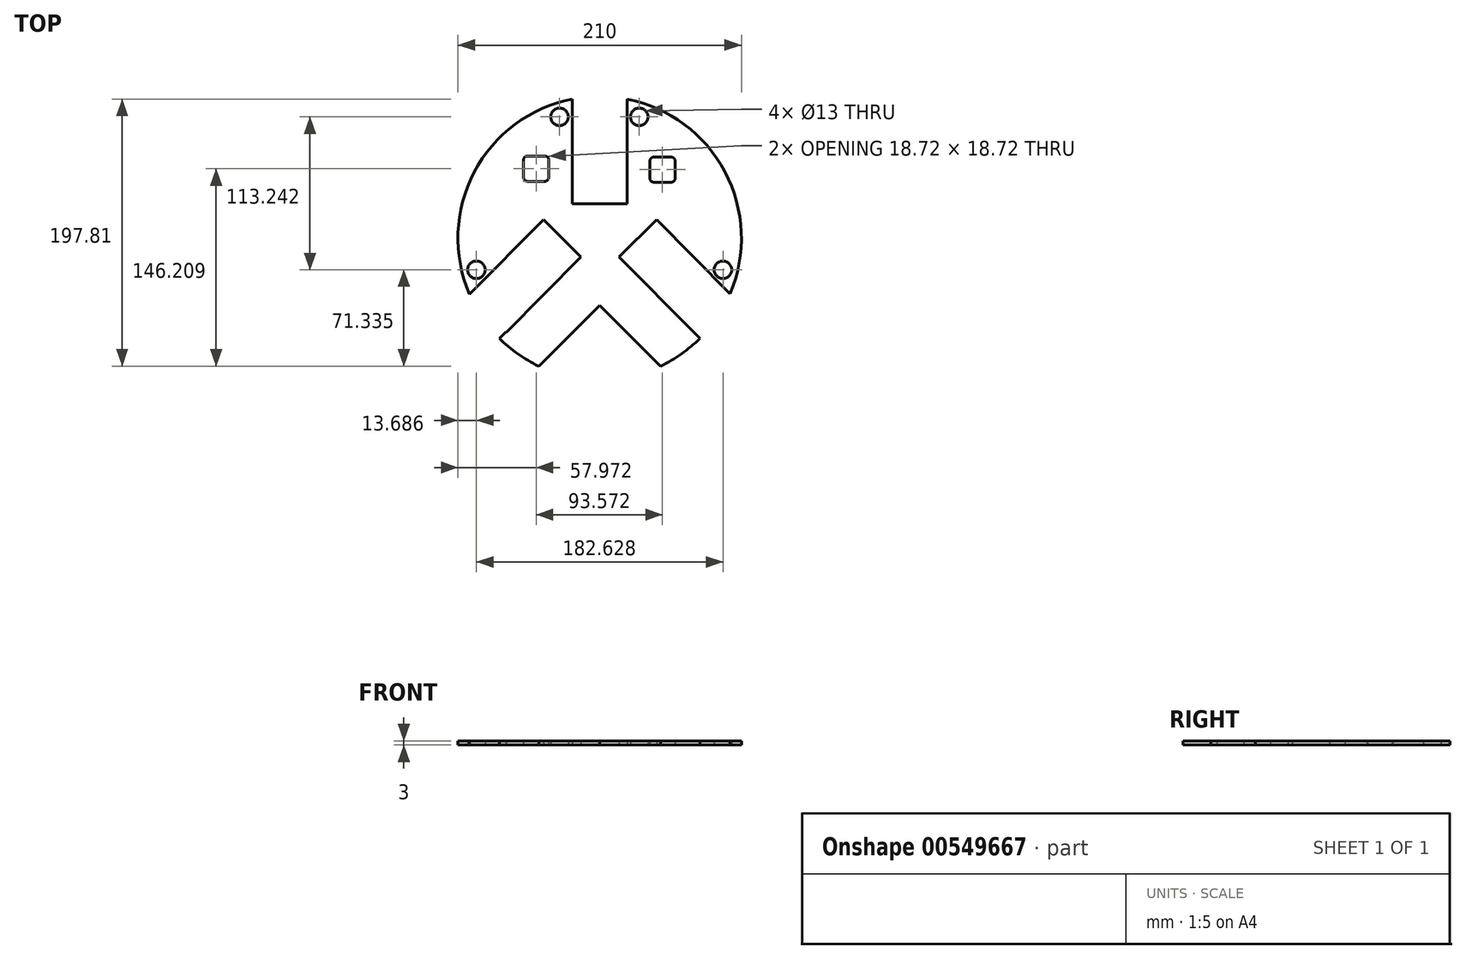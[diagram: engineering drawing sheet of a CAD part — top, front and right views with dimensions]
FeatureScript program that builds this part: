
annotation { "Feature Type Name" : "Feature", "Feature Type Description" : "" }
export const myFeature = defineFeature(function(context is Context, id is Id, definition is map)
    precondition{}
    {
        {
            var Q0;
            Q0=qCreatedBy(makeId("Top.planeOp"),FACE);
            var sketch = newSketch(context, id + "F0", { "sketchPlane" : qUnion([Q0])});
            skCircle(sketch, "E0", {"center": v(0, 0) * mm, "radius": 105 * mm});
            skLineSegment(sketch, "E1", {"start": v(0, 105) * mm, "end": v(0, -105) * mm});
            skLineSegment(sketch, "E2", {"start": v(0, 0) * mm, "end": v(-74.25, -74.25) * mm});
            skLineSegment(sketch, "E3", {"start": v(0, 0) * mm, "end": v(74.25, -74.25) * mm});
            skLineSegment(sketch, "E4", {"start": v(0, 0) * mm, "end": v(0, 105) * mm});
            skLineSegment(sketch, "E5", {"start": v(0, -49.67) * mm, "end": v(-45.13, -94.8) * mm});
            skLineSegment(sketch, "E6", {"start": v(0, -49.67) * mm, "end": v(45.13, -94.8) * mm});
            skLineSegment(sketch, "E7", {"start": v(-20.43, 103.99) * mm, "end": v(-0.4, 103.99) * mm});
            skLineSegment(sketch, "E8.bottom", {"start": v(-20.43, 103.99) * mm, "end": v(20.33, 103.99) * mm});
            skLineSegment(sketch, "E8.top", {"start": v(-20.43, 25.29) * mm, "end": v(20.33, 25.29) * mm});
            skLineSegment(sketch, "E8.left", {"start": v(-20.43, 103.99) * mm, "end": v(-20.43, 25.29) * mm});
            skLineSegment(sketch, "E8.right", {"start": v(20.33, 103.99) * mm, "end": v(20.33, 25.29) * mm});
            skLineSegment(sketch, "E9.bottom", {"start": v(-41.67, 13.74) * mm, "end": v(-13.83, -13.93) * mm});
            skLineSegment(sketch, "E9.top", {"start": v(-97.14, -42.09) * mm, "end": v(-69.3, -69.75) * mm});
            skLineSegment(sketch, "E9.left", {"start": v(-41.67, 13.74) * mm, "end": v(-97.14, -42.09) * mm});
            skLineSegment(sketch, "E9.right", {"start": v(-13.83, -13.93) * mm, "end": v(-69.3, -69.75) * mm});
            skLineSegment(sketch, "E10.bottom", {"start": v(14.3, -13.9) * mm, "end": v(42.15, 13.74) * mm});
            skLineSegment(sketch, "E10.top", {"start": v(69.75, -69.75) * mm, "end": v(97.6, -42.1) * mm});
            skLineSegment(sketch, "E10.left", {"start": v(14.3, -13.9) * mm, "end": v(69.75, -69.75) * mm});
            skLineSegment(sketch, "E10.right", {"start": v(42.15, 13.74) * mm, "end": v(97.6, -42.1) * mm});
            skLineSegment(sketch, "E11.bottom", {"start": v(-53.39, 60.77) * mm, "end": v(-40.67, 60.77) * mm});
            skLineSegment(sketch, "E11.top", {"start": v(-53.39, 42.05) * mm, "end": v(-40.67, 42.05) * mm});
            skLineSegment(sketch, "E11.left", {"start": v(-56.39, 57.77) * mm, "end": v(-56.39, 45.05) * mm});
            skLineSegment(sketch, "E11.right", {"start": v(-37.67, 57.77) * mm, "end": v(-37.67, 45.05) * mm});
            skLineSegment(sketch, "E12.bottom", {"start": v(40.18, 60.07) * mm, "end": v(52.9, 60.07) * mm});
            skLineSegment(sketch, "E12.top", {"start": v(40.18, 41.35) * mm, "end": v(52.9, 41.35) * mm});
            skLineSegment(sketch, "E12.left", {"start": v(37.18, 57.07) * mm, "end": v(37.18, 44.35) * mm});
            skLineSegment(sketch, "E12.right", {"start": v(55.9, 57.07) * mm, "end": v(55.9, 44.35) * mm});
            skCircle(sketch, "E13", {"center": v(-29.72, 89.78) * mm, "radius": 6.5 * mm});
            skCircle(sketch, "E14", {"center": v(29.3, 89.78) * mm, "radius": 6.5 * mm});
            skCircle(sketch, "E15", {"center": v(-91.31, -23.47) * mm, "radius": 6.5 * mm});
            skCircle(sketch, "E16", {"center": v(91.31, -23.47) * mm, "radius": 6.5 * mm});
            skPoint(sketch, "E17.visualSharp", {"position": v(-56.39, 60.77) * mm});
            skArc(sketch, "E17.filletArc", {"start": v(-53.39, 60.77) * mm, "mid": v(-55.5, 59.89) * mm, "end": v(-56.39, 57.77) * mm});
            skPoint(sketch, "E18.visualSharp", {"position": v(-37.67, 60.77) * mm});
            skArc(sketch, "E18.filletArc", {"start": v(-37.67, 57.77) * mm, "mid": v(-38.55, 59.89) * mm, "end": v(-40.67, 60.77) * mm});
            skPoint(sketch, "E19.visualSharp", {"position": v(-37.67, 42.05) * mm});
            skArc(sketch, "E19.filletArc", {"start": v(-40.67, 42.05) * mm, "mid": v(-38.55, 42.93) * mm, "end": v(-37.67, 45.05) * mm});
            skPoint(sketch, "E20.visualSharp", {"position": v(-56.39, 42.05) * mm});
            skArc(sketch, "E20.filletArc", {"start": v(-56.39, 45.05) * mm, "mid": v(-55.5, 42.93) * mm, "end": v(-53.39, 42.05) * mm});
            skPoint(sketch, "E21.visualSharp", {"position": v(37.18, 60.07) * mm});
            skArc(sketch, "E21.filletArc", {"start": v(40.18, 60.07) * mm, "mid": v(38.06, 59.19) * mm, "end": v(37.18, 57.07) * mm});
            skPoint(sketch, "E22.visualSharp", {"position": v(55.9, 60.07) * mm});
            skArc(sketch, "E22.filletArc", {"start": v(55.9, 57.07) * mm, "mid": v(55.03, 59.19) * mm, "end": v(52.9, 60.07) * mm});
            skPoint(sketch, "E23.visualSharp", {"position": v(55.9, 41.35) * mm});
            skArc(sketch, "E23.filletArc", {"start": v(52.9, 41.35) * mm, "mid": v(55.03, 42.23) * mm, "end": v(55.9, 44.35) * mm});
            skPoint(sketch, "E24.visualSharp", {"position": v(37.18, 41.35) * mm});
            skArc(sketch, "E24.filletArc", {"start": v(37.18, 44.35) * mm, "mid": v(38.06, 42.23) * mm, "end": v(40.18, 41.35) * mm});
            skLineSegment(sketch, "E25", {"start": v(0, -49.67) * mm, "end": v(0, -64.72) * mm});
            skLineSegment(sketch, "E26", {"start": v(-26.12, -75.8) * mm, "end": v(26.12, -75.8) * mm});
            skSolve(sketch);
        }
        {
            var Q0;
            Q0=makeQuery(id+"F0.imprint","IMPRINT",FACE,{"disambiguationData":[TD([[makeQuery(id+"F0.imprint","IMPRINT",EDGE,{"derivedFrom":sQuery(id+"F0.wireOp",EDGE,"E11.bottom")}),1.0]])]});
            var Q1;
            {var subQ6=sQuery(id+"F0.wireOp",EDGE,"E10.bottom");Q1=makeQuery(id+"F0.imprint","IMPRINT",FACE,{"disambiguationData":[TD([[makeQuery(id+"F0.imprint","IMPRINT",EDGE,{"derivedFrom":subQ6}),1.0]])]});}
            var Q2;
            {var subQ5=sQuery(id+"F0.wireOp",EDGE,"E9.right");Q2=makeQuery(id+"F0.imprint","IMPRINT",FACE,{"disambiguationData":[TD([[makeQuery(id+"F0.imprint","IMPRINT",EDGE,{"derivedFrom":subQ5}),1.0]])]});}
            var Q3;
            {var subQ0=sQuery(id+"F0.wireOp",EDGE,"E3");var subQ1=sQuery(id+"F0.wireOp",EDGE,"E0");var subQ2=makeQuery(id+"F0.imprint","INTERSECT",VERTEX,{"derivedFrom":[subQ1,subQ0]});Q3=makeQuery(id+"F0.imprint","IMPRINT",FACE,{"disambiguationData":[TD([[makeQuery(id+"F0.imprint","IMPRINT",EDGE,{"disambiguationData":[TD([[subQ2,1.0]])],"derivedFrom":subQ1}),1.0]])]});}
            var Q4;
            {var subQ0=sQuery(id+"F0.wireOp",EDGE,"E25");Q4=makeQuery(id+"F0.imprint","IMPRINT",FACE,{"disambiguationData":[TD([[makeQuery(id+"F0.imprint","IMPRINT",EDGE,{"derivedFrom":subQ0}),-1.0]])]});}
            var Q5;
            {var subQ0=sQuery(id+"F0.wireOp",EDGE,"E25");Q5=makeQuery(id+"F0.imprint","IMPRINT",FACE,{"disambiguationData":[TD([[makeQuery(id+"F0.imprint","IMPRINT",EDGE,{"derivedFrom":subQ0}),1.0]])]});}
            extrude(context, id + "F1", {"entities" : qUnion([Q0, Q1, Q2, Q3, Q4, Q5]), "depth" : 3 * mm, "offsetDistance" : 25.4 * mm});
        }
    });
